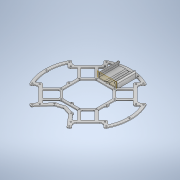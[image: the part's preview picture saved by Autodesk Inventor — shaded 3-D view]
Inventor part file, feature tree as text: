
AUTODESK INVENTOR PART (.ipt)
format: ipt  version: 2020 (Build 240168000, 168)  size: 1,259,520 bytes
history: native  units: mm
features: extrude x12, projected_geometry x12, sketch x8, other x3, fillet x2, chamfer x1
ambient origin geometry x8: Origin, YZ Plane, XZ Plane, XY Plane, X Axis, Y Axis, Z Axis, Center Point
bodies: Body1 (feature_tree)
feature tree (38):
  other  "Твердое тело1"
  extrude  "outer"  TaperAngle=45.0deg  [1 undecoded]
  extrude  "inner"  Depth=7.0mm
  sketch  "Эскиз3"
  extrude  "Выдавливание3"  Depth=20.0mm
  extrude  "Выдавливание4"  Depth=7.0mm
  sketch  "Эскиз4"
  extrude  "Выдавливание5"  Depth=3.2mm
  extrude  "Выдавливание6"  Depth=59.0mm
  sketch  "Эскиз5"
  extrude  "Выдавливание7"  Depth=83.0mm
  extrude  "Выдавливание8"  Depth=69.0mm
  sketch  "Эскиз6"
  extrude  "Выдавливание9"  Depth=55.0mm
  extrude  "Выдавливание10"  Depth=3.0mm
  other  "РабПлоскость1"
  extrude  "Выдавливание11"  Depth=8.0mm
  chamfer  "Фаска1"  Distance=5.0mm
  fillet  "Сопряжение1"  Radius=2.0mm
  fillet  "Сопряжение2"  Radius=40.0mm
  other  "РабПлоскость2"
  extrude  "Выдавливание12"  Depth=2.0mm
  sketch  "Эскиз1"
  sketch  "Эскиз2"
  projected_geometry  "Спроецированная петля1"
  projected_geometry  "Спроецированная петля2"
  projected_geometry  "Спроецированная петля3"
  projected_geometry  "Спроецированная петля4"
  projected_geometry  "Спроецированная петля5"
  sketch  "Эскиз7"
  projected_geometry  "Спроецированная петля6"
  projected_geometry  "Спроецированная петля7"
  projected_geometry  "Спроецированная петля8"
  sketch  "Эскиз8"
  projected_geometry  "Спроецированная петля9"
  projected_geometry  "Спроецированная петля10"
  projected_geometry  "Спроецированная петля11"
  projected_geometry  "Спроецированная петля12"
note: 1 required parameter value undecoded (feature->parameter linkage not recoverable at this tier; creation-order binding heuristic only, values carry confidence <= 0.55)
